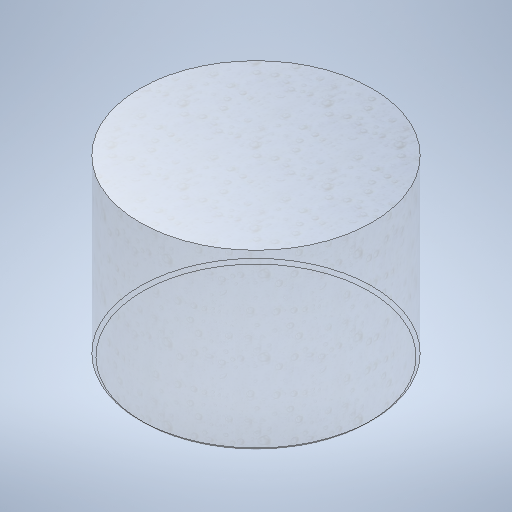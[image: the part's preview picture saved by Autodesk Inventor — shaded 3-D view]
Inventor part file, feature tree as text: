
AUTODESK INVENTOR PART (.ipt)
format: ipt  version: 2025.2 (Build 292293000, 293)  size: 315,392 bytes
history: native  units: mm
features: extrude x1, fillet x1, sketch x1
ambient origin geometry x8: Origin, YZ Plane, XZ Plane, XY Plane, X Axis, Y Axis, Z Axis, Center Point
bodies: Solid1 (feature_tree)
feature tree (3):
  extrude  "Extrusion1"  Depth=60.0mm TaperAngle=0.0deg
  fillet  "Fillet1"  Radius=1.0mm
  sketch  "Sketch1"  dims[d0=80.0mm d1=60.0mm d2=0.0mm d3=1.0mm]
